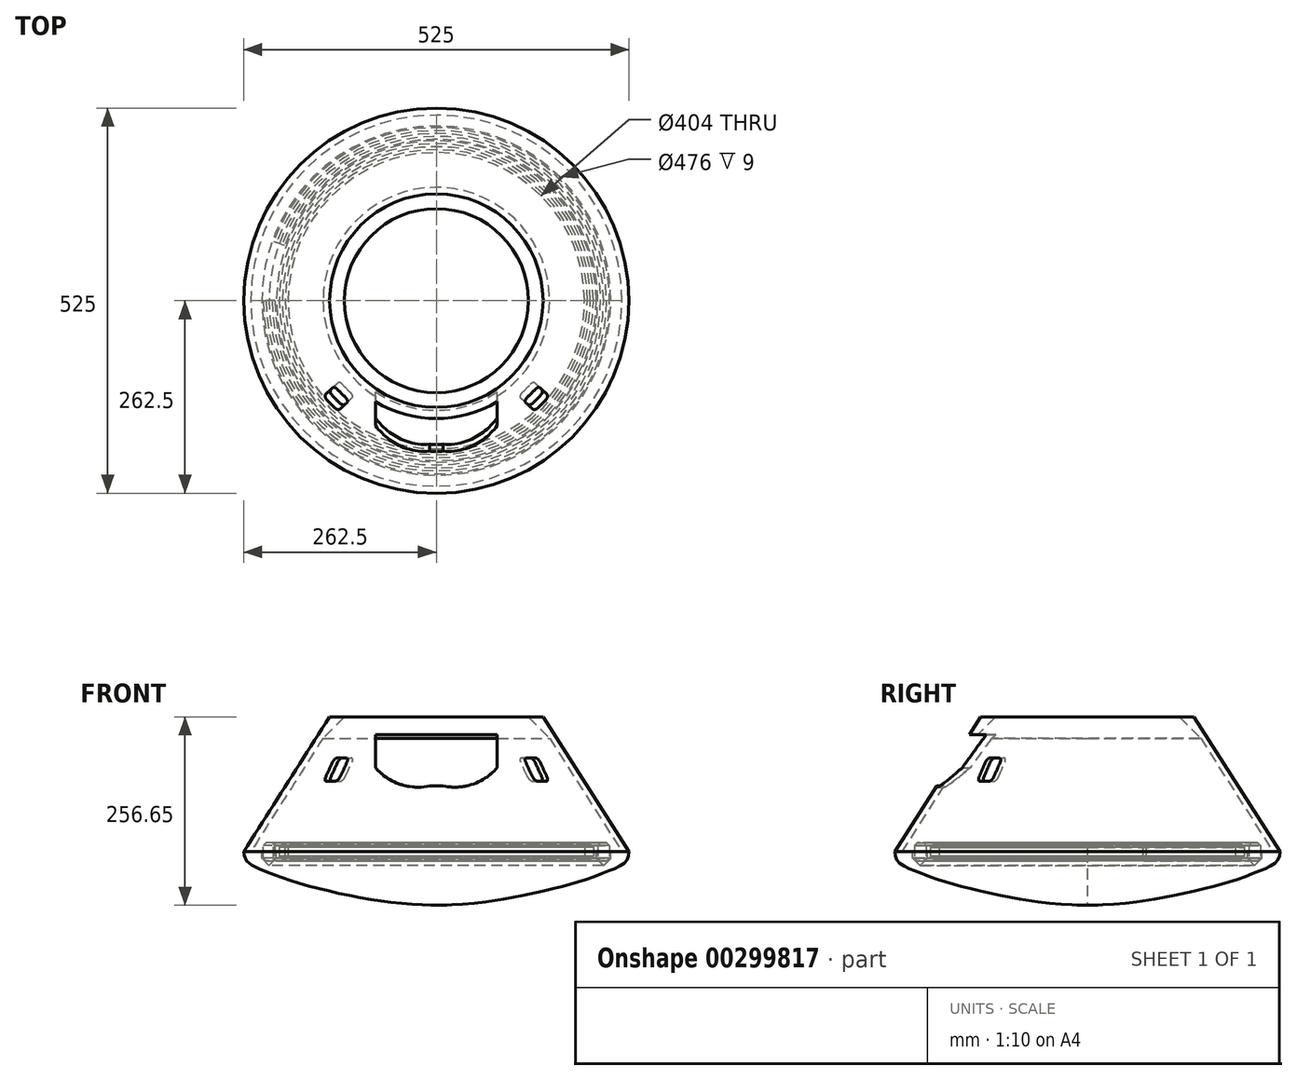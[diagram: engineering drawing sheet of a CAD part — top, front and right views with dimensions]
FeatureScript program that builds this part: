
annotation { "Feature Type Name" : "Feature", "Feature Type Description" : "" }
export const myFeature = defineFeature(function(context is Context, id is Id, definition is map)
    precondition{}
    {
        {
            var Q0;
            Q0=qCreatedBy(makeId("Front.planeOp"),FACE);
            var sketch = newSketch(context, id + "F0", { "sketchPlane" : qUnion([Q0])});
            skLineSegment(sketch, "E0", {"start": v(0, 0) * mm, "end": v(0, 219.9) * mm});
            skLineSegment(sketch, "E1", {"start": v(156, 0) * mm, "end": v(156, 199.27) * mm});
            skSolve(sketch);
        }
        {
            var Q0;
            Q0=qCreatedBy(makeId("Front.planeOp"),FACE);
            var sketch = newSketch(context, id + "F1", { "sketchPlane" : qUnion([Q0])});
            skLineSegment(sketch, "E2", {"start": v(0, 0) * mm, "end": v(0, -73) * mm});
            skPoint(sketch, "E3.3.internal.snap0", {"position": v(0, -36.5) * mm});
            skLineSegment(sketch, "E4.MirrorCS", {"start": v(0, 0) * mm, "end": v(-218, 0) * mm});
            skFitSpline(sketch, "E5.MirrorCS", {"points": [v(-262.5, 0) * mm, v(-260.28, -10.3) * mm, v(-234.8, -26.39) * mm, v(-200.67, -38.94) * mm, v(-152.59, -52.2) * mm, v(-92.48, -64.7) * mm, v(-36.32, -71.32) * mm, v(0, -73) * mm], "startDerivative": vector(0.74, -23.91) * mm, "endDerivative": vector(97.44, 1.08) * mm});
            skLineSegment(sketch, "E6", {"start": v(-238, 0) * mm, "end": v(-262.5, 0) * mm});
            skLineSegment(sketch, "E7", {"start": v(-238, 0) * mm, "end": v(-238, -9) * mm});
            skLineSegment(sketch, "E8", {"start": v(-238, -9) * mm, "end": v(-228, -19) * mm});
            skLineSegment(sketch, "E9", {"start": v(-228, -19) * mm, "end": v(-228, -11.28) * mm});
            skLineSegment(sketch, "E10.MirrorCS", {"start": v(-218, -9) * mm, "end": v(-228, -19) * mm});
            skLineSegment(sketch, "E11.MirrorCS", {"start": v(-218, 0) * mm, "end": v(-218, -9) * mm});
            skSolve(sketch);
        }
        {
            var Q0;
            Q0 = qSketchRegion(id + "F1", true);
            var Q1;
            Q1=sQuery(id+"F1.wireOp",EDGE,"E2");
            revolve(context, id + "F2", {"surfaceOperationType" : NewSurfaceOperationType.NEW, "entities" : qUnion([Q0]), "axis" : qUnion([Q1]), "revolveType" : RevolveType.FULL});
        }
        {
            var Q0;
            Q0=makeQuery(id+"F2.opRevolve","SWEPT_FACE",FACE,{"disambiguationData":[OSD([sQuery(id+"F1.wireOp",EDGE,"E4.MirrorCS")])]});
            var sketch = newSketch(context, id + "F3", { "sketchPlane" : qUnion([Q0])});
            skCircle(sketch, "E12", {"center": v(0, 0) * mm, "radius": 202 * mm});
            skCircle(sketch, "E13", {"center": v(0, 0) * mm, "radius": 214 * mm});
            skSolve(sketch);
        }
        {
            var Q0;
            Q0 = qSketchRegion(id + "F3", true);
            extrude(context, id + "F4", {"entities" : qUnion([Q0]), "depth" : 20 * mm, "offsetDistance" : 25 * mm, "symmetric" : true});
        }
        {
            var Q0;
            Q0=makeQuery(id+"F4.opExtrude","CAP_FACE",FACE,{"disambiguationData":[OSD([sQuery(id+"F3.wireOp",EDGE,"E12"),sQuery(id+"F3.wireOp",EDGE,"E13")])],"isStart":false});
            var Q1;
            Q1=makeQuery(id+"F4.opExtrude","CAP_FACE",FACE,{"disambiguationData":[OSD([sQuery(id+"F3.wireOp",EDGE,"E12"),sQuery(id+"F3.wireOp",EDGE,"E13")])],"isStart":true});
            chamfer(context, id + "F5", {"entities" : qUnion([Q0, Q1]), "width" : 4 * mm, "tangentPropagation" : true});
        }
        {
            var Q0;
            Q0=qCreatedBy(makeId("Front.planeOp"),FACE);
            var sketch = newSketch(context, id + "F6", { "sketchPlane" : qUnion([Q0])});
            skLineSegment(sketch, "E14.MirrorCS", {"start": v(-218, 0) * mm, "end": v(0, 0) * mm});
            skLineSegment(sketch, "E15.MirrorCS", {"start": v(-218, 9) * mm, "end": v(-218, 0) * mm});
            skLineSegment(sketch, "E16.MirrorCS", {"start": v(-238, 9) * mm, "end": v(-238, 0) * mm});
            skLineSegment(sketch, "E17.MirrorCS", {"start": v(-262.5, 0) * mm, "end": v(-238, 0) * mm});
            skLineSegment(sketch, "E18", {"start": v(-262.5, 0) * mm, "end": v(-145.5, 183.65) * mm});
            skLineSegment(sketch, "E19", {"start": v(-262.5, 0) * mm, "end": v(-262.5, 92.46) * mm});
            skLineSegment(sketch, "E20", {"start": v(-145.5, 183.65) * mm, "end": v(0, 183.65) * mm});
            skLineSegment(sketch, "E21", {"start": v(-136.01, 183.65) * mm, "end": v(-253.01, 0) * mm});
            skLineSegment(sketch, "E22", {"start": v(-218, 9) * mm, "end": v(-228, 19) * mm});
            skLineSegment(sketch, "E23", {"start": v(-228, 19) * mm, "end": v(-228, 12.2) * mm});
            skLineSegment(sketch, "E24.MirrorCS", {"start": v(-238, 9) * mm, "end": v(-228, 19) * mm});
            skLineSegment(sketch, "E25", {"start": v(-154.47, 154.68) * mm, "end": v(-125.5, 183.65) * mm});
            skSolve(sketch);
        }
        {
            var Q0;
            Q0 = qSketchRegion(id + "F6", true);
            var Q1;
            Q1=sQuery(id+"F0.wireOp",EDGE,"E0");
            revolve(context, id + "F7", {"surfaceOperationType" : NewSurfaceOperationType.NEW, "entities" : qUnion([Q0]), "axis" : qUnion([Q1]), "revolveType" : RevolveType.FULL});
        }
        {
            var Q0;
            Q0=qCreatedBy(makeId("Front.planeOp"),FACE);
            var sketch = newSketch(context, id + "F8", { "sketchPlane" : qUnion([Q0])});
            skLineSegment(sketch, "E26", {"start": v(0, 89.65) * mm, "end": v(0, 159.65) * mm});
            skLineSegment(sketch, "E27", {"start": v(0, 159.65) * mm, "end": v(83, 159.65) * mm});
            skLineSegment(sketch, "E28", {"start": v(83, 159.65) * mm, "end": v(83, 114.65) * mm});
            skLineSegment(sketch, "E29", {"start": v(0, 89.65) * mm, "end": v(9, 89.65) * mm});
            skArc(sketch, "E30", {"start": v(9, 89.65) * mm, "mid": v(49.45, 91.93) * mm, "end": v(83, 114.65) * mm});
            skLineSegment(sketch, "E31.MirrorCS", {"start": v(-83, 159.65) * mm, "end": v(-83, 114.65) * mm});
            skLineSegment(sketch, "E32.MirrorCS", {"start": v(0, 159.65) * mm, "end": v(-83, 159.65) * mm});
            skArc(sketch, "E33.MirrorCS", {"start": v(-9, 89.65) * mm, "mid": v(-49.45, 91.93) * mm, "end": v(-83, 114.65) * mm});
            skLineSegment(sketch, "E34.MirrorCS", {"start": v(0, 89.65) * mm, "end": v(-9, 89.65) * mm});
            skSolve(sketch);
        }
        {
            var Q0;
            Q0 = qSketchRegion(id + "F8", true);
            extrude(context, id + "F9", {"entities" : qUnion([Q0]), "operationType" : NewBodyOperationType.REMOVE, "depth" : 500 * mm, "offsetDistance" : 25 * mm});
        }
        {
            var Q0;
            Q0=qCreatedBy(makeId("Front.planeOp"),FACE);
            var sketch = newSketch(context, id + "F10", { "sketchPlane" : qUnion([Q0])});
            skLineSegment(sketch, "E35", {"start": v(0, 112) * mm, "end": v(0, 128) * mm});
            skLineSegment(sketch, "E36", {"start": v(0, 128) * mm, "end": v(8, 128) * mm});
            skLineSegment(sketch, "E37", {"start": v(0, 112) * mm, "end": v(14, 112) * mm});
            skLineSegment(sketch, "E38", {"start": v(14, 112) * mm, "end": v(14, 122) * mm});
            skArc(sketch, "E39", {"start": v(14, 122) * mm, "mid": v(12.24, 126.24) * mm, "end": v(8, 128) * mm});
            skLineSegment(sketch, "E40.MirrorCS", {"start": v(0, 112) * mm, "end": v(-14, 112) * mm});
            skLineSegment(sketch, "E41.MirrorCS", {"start": v(0, 128) * mm, "end": v(-8, 128) * mm});
            skArc(sketch, "E42.MirrorCS", {"start": v(-14, 122) * mm, "mid": v(-12.24, 126.24) * mm, "end": v(-8, 128) * mm});
            skLineSegment(sketch, "E43.MirrorCS", {"start": v(-14, 112) * mm, "end": v(-14, 122) * mm});
            skLineSegment(sketch, "E44.MirrorCS", {"start": v(14, 112) * mm, "end": v(14, 102) * mm});
            skLineSegment(sketch, "E45.MirrorCS", {"start": v(0, 96) * mm, "end": v(-8, 96) * mm});
            skLineSegment(sketch, "E46.MirrorCS", {"start": v(0, 96) * mm, "end": v(8, 96) * mm});
            skArc(sketch, "E47.MirrorCS", {"start": v(-14, 102) * mm, "mid": v(-12.24, 97.76) * mm, "end": v(-8, 96) * mm});
            skLineSegment(sketch, "E48.MirrorCS", {"start": v(-14, 112) * mm, "end": v(-14, 102) * mm});
            skArc(sketch, "E49.MirrorCS", {"start": v(14, 102) * mm, "mid": v(12.24, 97.76) * mm, "end": v(8, 96) * mm});
            skLineSegment(sketch, "E50.MirrorCS", {"start": v(0, 112) * mm, "end": v(0, 96) * mm});
            skSolve(sketch);
        }
        {
            var Q0;
            Q0 = qSketchRegion(id + "F10", true);
            extrude(context, id + "F11", {"entities" : qUnion([Q0]), "depth" : 200 * mm, "offsetDistance" : 25 * mm});
        }
        {
            var Q0;
            Q0=makeQuery(id+"F11.opExtrude","SWEPT_BODY",BODY,{"disambiguationData":[OSD([sQuery(id+"F10.wireOp",EDGE,"E36"),sQuery(id+"F10.wireOp",EDGE,"E38"),sQuery(id+"F10.wireOp",EDGE,"E39"),sQuery(id+"F10.wireOp",EDGE,"E41.MirrorCS"),sQuery(id+"F10.wireOp",EDGE,"E42.MirrorCS"),sQuery(id+"F10.wireOp",EDGE,"E43.MirrorCS"),sQuery(id+"F10.wireOp",EDGE,"E44.MirrorCS"),sQuery(id+"F10.wireOp",EDGE,"E45.MirrorCS"),sQuery(id+"F10.wireOp",EDGE,"E46.MirrorCS"),sQuery(id+"F10.wireOp",EDGE,"E47.MirrorCS"),sQuery(id+"F10.wireOp",EDGE,"E48.MirrorCS"),sQuery(id+"F10.wireOp",EDGE,"E49.MirrorCS")])]});
            var Q1;
            Q1=makeQuery(id+"F11.opExtrude","CAP_EDGE",EDGE,{"disambiguationData":[OSD([sQuery(id+"F10.wireOp",EDGE,"E38"),sQuery(id+"F10.wireOp",EDGE,"E44.MirrorCS")])],"isStart":true});
            transform(context, id + "F12", {"entities" : qUnion([Q0]), "transformType" : TransformType.ROTATION, "transformAxis" : qUnion([Q1]), "angle" : 47 * degree, "makeCopy" : true});
        }
        {
            var Q0;
            Q0=makeQuery(id+"F11.opExtrude","SWEPT_BODY",BODY,{"disambiguationData":[OSD([sQuery(id+"F10.wireOp",EDGE,"E36"),sQuery(id+"F10.wireOp",EDGE,"E38"),sQuery(id+"F10.wireOp",EDGE,"E39"),sQuery(id+"F10.wireOp",EDGE,"E41.MirrorCS"),sQuery(id+"F10.wireOp",EDGE,"E42.MirrorCS"),sQuery(id+"F10.wireOp",EDGE,"E43.MirrorCS"),sQuery(id+"F10.wireOp",EDGE,"E44.MirrorCS"),sQuery(id+"F10.wireOp",EDGE,"E45.MirrorCS"),sQuery(id+"F10.wireOp",EDGE,"E46.MirrorCS"),sQuery(id+"F10.wireOp",EDGE,"E47.MirrorCS"),sQuery(id+"F10.wireOp",EDGE,"E48.MirrorCS"),sQuery(id+"F10.wireOp",EDGE,"E49.MirrorCS")])]});
            var Q1;
            Q1=makeQuery(id+"F11.opExtrude","CAP_EDGE",EDGE,{"disambiguationData":[OSD([sQuery(id+"F10.wireOp",EDGE,"E43.MirrorCS"),sQuery(id+"F10.wireOp",EDGE,"E48.MirrorCS")])],"isStart":true});
            transform(context, id + "F13", {"entities" : qUnion([Q0]), "transformType" : TransformType.ROTATION, "transformAxis" : qUnion([Q1]), "angle" : 47 * degree, "oppositeDirection" : true, "makeCopy" : false});
        }
        {
            var Q0;
            Q0=makeQuery(id+"F11.opExtrude","SWEPT_BODY",BODY,{"disambiguationData":[OSD([sQuery(id+"F10.wireOp",EDGE,"E36"),sQuery(id+"F10.wireOp",EDGE,"E38"),sQuery(id+"F10.wireOp",EDGE,"E39"),sQuery(id+"F10.wireOp",EDGE,"E41.MirrorCS"),sQuery(id+"F10.wireOp",EDGE,"E42.MirrorCS"),sQuery(id+"F10.wireOp",EDGE,"E43.MirrorCS"),sQuery(id+"F10.wireOp",EDGE,"E44.MirrorCS"),sQuery(id+"F10.wireOp",EDGE,"E45.MirrorCS"),sQuery(id+"F10.wireOp",EDGE,"E46.MirrorCS"),sQuery(id+"F10.wireOp",EDGE,"E47.MirrorCS"),sQuery(id+"F10.wireOp",EDGE,"E48.MirrorCS"),sQuery(id+"F10.wireOp",EDGE,"E49.MirrorCS")])]});
            var Q1;
            Q1=makeQuery(id+"F12.opPattern","COPY",BODY,{"derivedFrom":makeQuery(id+"F11.opExtrude","SWEPT_BODY",BODY,{"disambiguationData":[OSD([sQuery(id+"F10.wireOp",EDGE,"E36"),sQuery(id+"F10.wireOp",EDGE,"E38"),sQuery(id+"F10.wireOp",EDGE,"E39"),sQuery(id+"F10.wireOp",EDGE,"E41.MirrorCS"),sQuery(id+"F10.wireOp",EDGE,"E42.MirrorCS"),sQuery(id+"F10.wireOp",EDGE,"E43.MirrorCS"),sQuery(id+"F10.wireOp",EDGE,"E44.MirrorCS"),sQuery(id+"F10.wireOp",EDGE,"E45.MirrorCS"),sQuery(id+"F10.wireOp",EDGE,"E46.MirrorCS"),sQuery(id+"F10.wireOp",EDGE,"E47.MirrorCS"),sQuery(id+"F10.wireOp",EDGE,"E48.MirrorCS"),sQuery(id+"F10.wireOp",EDGE,"E49.MirrorCS")])]}),"instanceName":"1"});
            var Q2;
            Q2=makeQuery(id+"F7.opRevolve","SWEPT_BODY",BODY,{"disambiguationData":[OSD([sQuery(id+"F6.wireOp",EDGE,"E17.MirrorCS"),sQuery(id+"F6.wireOp",EDGE,"E18"),sQuery(id+"F6.wireOp",EDGE,"E20"),sQuery(id+"F6.wireOp",EDGE,"E21")])]});
            booleanBodies(context, id + "F14", {"operationType" : BooleanOperationType.SUBTRACTION, "tools" : qUnion([Q0, Q1]), "targets" : qUnion([Q2])});
        }
        {
            var Q0;
            Q0=qCreatedBy(makeId("Front.planeOp"),FACE);
            cPlane(context, id + "F15", {"entities" : qUnion([Q0]), "cplaneType" : CPlaneType.OFFSET, "offset" : 233.5 * mm, "width" : 150 * mm, "height" : 150 * mm});
        }
        {
            var Q0;
            Q0=qCreatedBy(makeId("Front.planeOp"),FACE);
            var sketch = newSketch(context, id + "F16", { "sketchPlane" : qUnion([Q0])});
            skLineSegment(sketch, "E51", {"start": v(-220, 0) * mm, "end": v(-220, 8.5) * mm});
            skLineSegment(sketch, "E52", {"start": v(-220, 8.5) * mm, "end": v(-224, 12.5) * mm});
            skLineSegment(sketch, "E53", {"start": v(-224, 12.5) * mm, "end": v(-228, 12.5) * mm});
            skLineSegment(sketch, "E54.MirrorCS", {"start": v(-232, 12.5) * mm, "end": v(-228, 12.5) * mm});
            skLineSegment(sketch, "E55.MirrorCS", {"start": v(-236, 8.5) * mm, "end": v(-232, 12.5) * mm});
            skLineSegment(sketch, "E56.MirrorCS", {"start": v(-236, 0) * mm, "end": v(-236, 8.5) * mm});
            skLineSegment(sketch, "E57.MirrorCS", {"start": v(-220, 0) * mm, "end": v(-220, -8.5) * mm});
            skLineSegment(sketch, "E58.MirrorCS", {"start": v(-220, -8.5) * mm, "end": v(-224, -12.5) * mm});
            skLineSegment(sketch, "E59.MirrorCS", {"start": v(-224, -12.5) * mm, "end": v(-228, -12.5) * mm});
            skLineSegment(sketch, "E60.MirrorCS", {"start": v(-232, -12.5) * mm, "end": v(-228, -12.5) * mm});
            skLineSegment(sketch, "E61.MirrorCS", {"start": v(-236, -8.5) * mm, "end": v(-232, -12.5) * mm});
            skLineSegment(sketch, "E62.MirrorCS", {"start": v(-236, 0) * mm, "end": v(-236, -8.5) * mm});
            skSolve(sketch);
        }
        {
            var Q0;
            Q0 = qSketchRegion(id + "F16", true);
            var Q1;
            Q1=sQuery(id+"F0.wireOp",EDGE,"E0");
            revolve(context, id + "F17", {"surfaceOperationType" : NewSurfaceOperationType.NEW, "entities" : qUnion([Q0]), "axis" : qUnion([Q1]), "revolveType" : RevolveType.ONE_DIRECTION, "angle" : 340 * degree});
        }
    });
